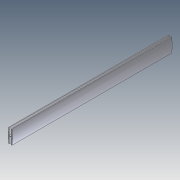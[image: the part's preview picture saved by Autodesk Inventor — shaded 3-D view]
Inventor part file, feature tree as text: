
AUTODESK INVENTOR PART (.ipt)
format: ipt  version: 2012 (Build 160160000, 160)  size: 88,576 bytes
history: native  units: in
note: dims shown in document units (in); Inventor stores cm internally (conversion verified against a paired STEP export)
features: extrude x1, sketch x1
ambient origin geometry x8: Origin, YZ Plane, XZ Plane, XY Plane, X Axis, Y Axis, Z Axis, Center Point
bodies: Solid1 (feature_tree)
feature tree (2):
  extrude  "Extrusion1"  Depth=0.0781in
  sketch  "Sketch1"  dims[d0=0.5234in d1=1.0469in d2=0.0781in d3=0.1562in d4=0.0781in d5=0.1562in d6=0.0234in d7=0.0469in d8=0.5234in d9=1.0469in d10=4.0in d12=0.0469in d13=12.0in d14=0.0in]
